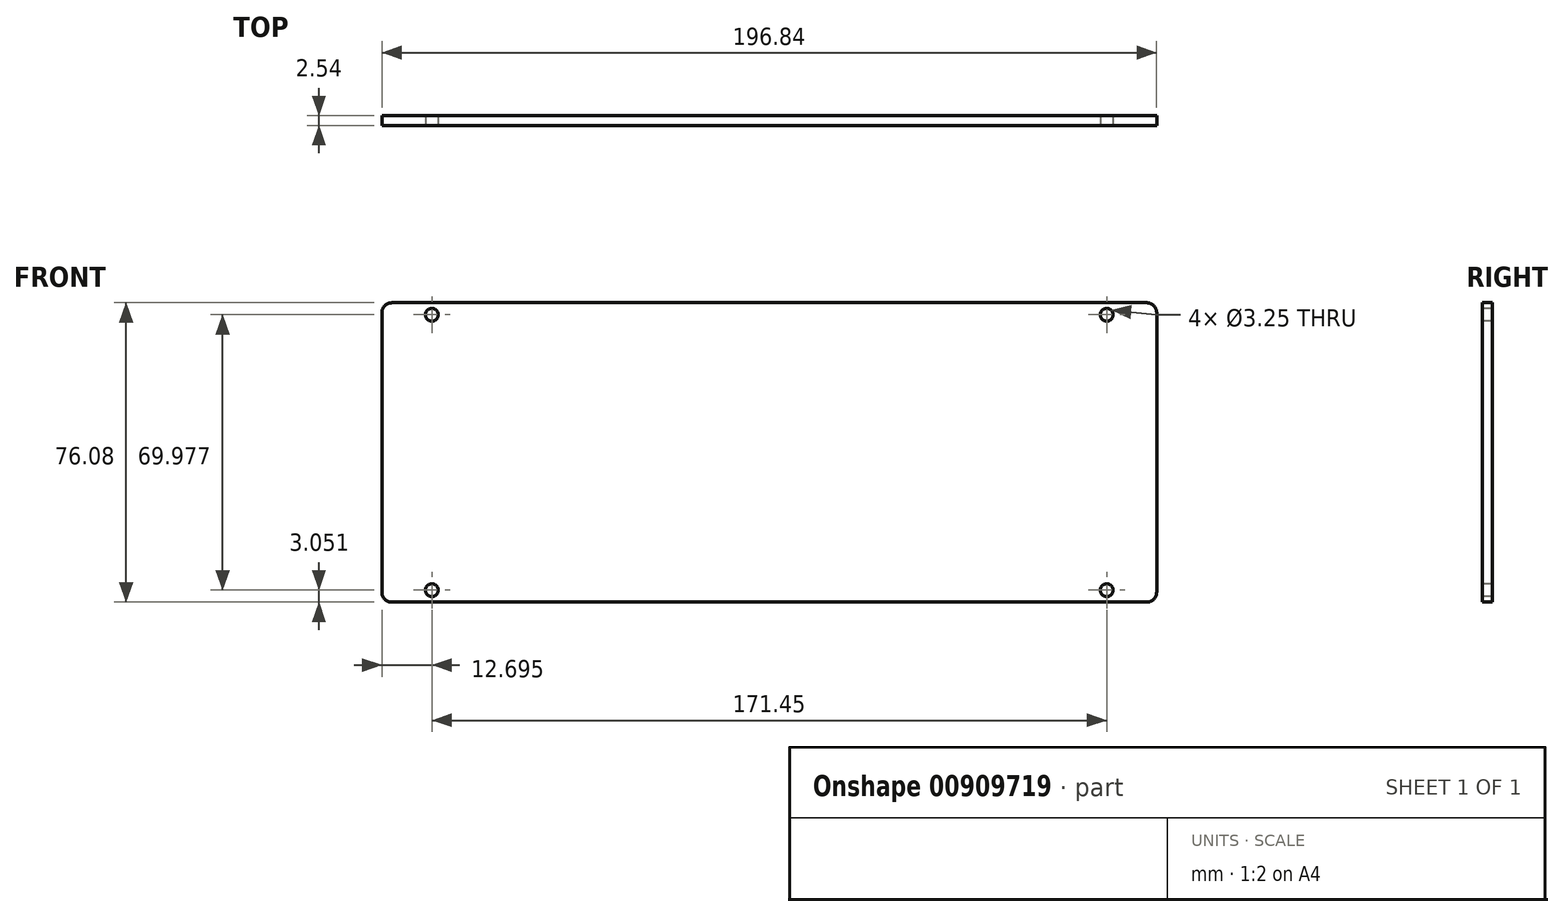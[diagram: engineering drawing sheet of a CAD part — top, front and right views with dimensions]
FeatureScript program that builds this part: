
annotation { "Feature Type Name" : "Feature", "Feature Type Description" : "" }
export const myFeature = defineFeature(function(context is Context, id is Id, definition is map)
    precondition{}
    {
        {
            var Q0;
            Q0=qCreatedBy(makeId("Front.planeOp"),FACE);
            var sketch = newSketch(context, id + "F0", { "sketchPlane" : qUnion([Q0])});
            skLineSegment(sketch, "E0.bottom", {"start": v(98.42, 38.04) * mm, "end": v(-98.43, 38.04) * mm});
            skLineSegment(sketch, "E0.top", {"start": v(98.43, -38.04) * mm, "end": v(-98.42, -38.04) * mm});
            skLineSegment(sketch, "E0.left", {"start": v(98.42, 38.04) * mm, "end": v(98.43, -38.04) * mm});
            skLineSegment(sketch, "E0.right", {"start": v(-98.43, 38.04) * mm, "end": v(-98.42, -38.04) * mm});
            skPoint(sketch, "E0.middle", {"position": v(0, 0) * mm});
            skSolve(sketch);
        }
        {
            var Q0;
            Q0=makeQuery(id+"F0.imprint","IMPRINT",FACE,{"disambiguationData":[TD([[makeQuery(id+"F0.imprint","IMPRINT",EDGE,{"derivedFrom":sQuery(id+"F0.wireOp",EDGE,"E0.bottom")}),1.0]])]});
            extrude(context, id + "F1", {"entities" : qUnion([Q0]), "endBound" : BoundingType.SYMMETRIC, "depth" : 2.54 * mm, "offsetDistance" : 25.4 * mm});
        }
        {
            var Q0;
            Q0=makeQuery(id+"F1.opExtrude","SWEPT_EDGE",EDGE,{"disambiguationData":[OSD([sQuery(id+"F0.wireOp",EDGE,"E0.bottom"),sQuery(id+"F0.wireOp",EDGE,"E0.right")])]});
            var Q1;
            Q1=makeQuery(id+"F1.opExtrude","SWEPT_EDGE",EDGE,{"disambiguationData":[OSD([sQuery(id+"F0.wireOp",EDGE,"E0.top"),sQuery(id+"F0.wireOp",EDGE,"E0.right")])]});
            var Q2;
            Q2=makeQuery(id+"F1.opExtrude","SWEPT_EDGE",EDGE,{"disambiguationData":[OSD([sQuery(id+"F0.wireOp",EDGE,"E0.top"),sQuery(id+"F0.wireOp",EDGE,"E0.left")])]});
            var Q3;
            Q3=makeQuery(id+"F1.opExtrude","SWEPT_EDGE",EDGE,{"disambiguationData":[OSD([sQuery(id+"F0.wireOp",EDGE,"E0.bottom"),sQuery(id+"F0.wireOp",EDGE,"E0.left")])]});
            fillet(context, id + "F2", {"entities" : qUnion([Q0, Q1, Q2, Q3]), "radius" : 2.54 * mm, "tangentPropagation" : true, "allowEdgeOverflow" : false});
        }
        {
            var Q0;
            Q0=makeQuery(id+"F1.opExtrude","CAP_FACE",FACE,{"disambiguationData":[OSD([sQuery(id+"F0.wireOp",EDGE,"E0.bottom"),sQuery(id+"F0.wireOp",EDGE,"E0.top"),sQuery(id+"F0.wireOp",EDGE,"E0.left"),sQuery(id+"F0.wireOp",EDGE,"E0.right")])],"isStart":false});
            var sketch = newSketch(context, id + "F3", { "sketchPlane" : qUnion([Q0])});
            skLineSegment(sketch, "E1", {"start": v(98.43, 31.6) * mm, "end": v(85.73, 31.6) * mm});
            skLineSegment(sketch, "E2", {"start": v(85.72, 38.04) * mm, "end": v(85.72, 34.99) * mm});
            skLineSegment(sketch, "E3.MirrorCS", {"start": v(-85.72, 38.04) * mm, "end": v(-85.72, 34.99) * mm});
            skLineSegment(sketch, "E4.MirrorCS", {"start": v(-85.72, -38.04) * mm, "end": v(-85.72, -34.99) * mm});
            skLineSegment(sketch, "E5.MirrorCS", {"start": v(85.72, -38.04) * mm, "end": v(85.72, -34.99) * mm});
            skSolve(sketch);
        }
        {
            var Q0;
            Q0=sQuery(id+"F3.wireOp",VERTEX,"E2.end");
            var Q1;
            Q1=sQuery(id+"F3.wireOp",VERTEX,"E5.MirrorCS.end");
            var Q2;
            Q2=sQuery(id+"F3.wireOp",VERTEX,"E4.MirrorCS.end");
            var Q3;
            Q3=sQuery(id+"F3.wireOp",VERTEX,"E3.MirrorCS.end");
            var Q4;
            Q4=makeQuery(id+"F1.opExtrude","SWEPT_BODY",BODY,{"disambiguationData":[OSD([sQuery(id+"F0.wireOp",EDGE,"E0.bottom"),sQuery(id+"F0.wireOp",EDGE,"E0.top"),sQuery(id+"F0.wireOp",EDGE,"E0.left"),sQuery(id+"F0.wireOp",EDGE,"E0.right")])]});
            hole(context, id + "F4", {"style" : HoleStyle.SIMPLE, "endStyle" : HoleEndStyle.THROUGH, "standardTappedOrClearance" : lookupTablePath({ "fit" : "Normal (ASME)", "standard" : "ANSI", "size" : "#4", "type" : "Clearance" }), "standardBlindInLast" : lookupTablePath({ "fit" : "Normal", "standard" : "ANSI", "size" : "#4", "type" : "Clearance" }), "holeDiameter" : 3.25 * mm, "majorDiameter" : 2.84 * mm, "isTappedThrough" : true, "tappedDepth" : 12.7 * mm, "tapClearance" : 3, "locations" : qUnion([Q0, Q1, Q2, Q3]), "scope" : qUnion([Q4])});
        }
    });
